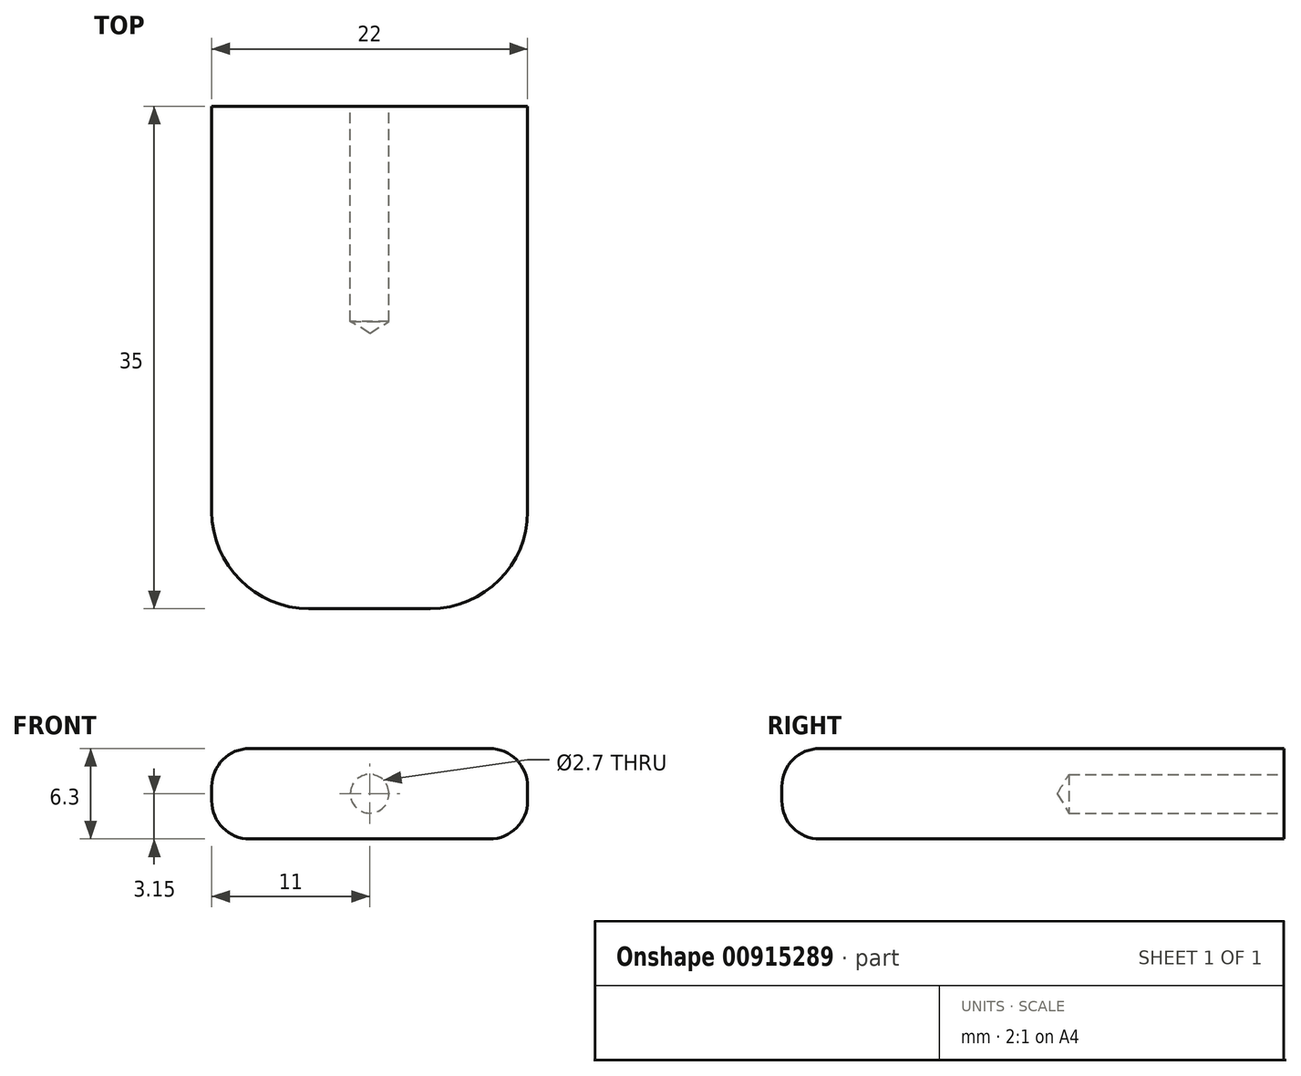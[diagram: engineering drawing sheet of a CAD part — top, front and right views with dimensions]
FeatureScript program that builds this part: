
annotation { "Feature Type Name" : "Feature", "Feature Type Description" : "" }
export const myFeature = defineFeature(function(context is Context, id is Id, definition is map)
    precondition{}
    {
        {
            var Q0;
            Q0=qCreatedBy(makeId("Top.planeOp"),FACE);
            var sketch = newSketch(context, id + "F0", { "sketchPlane" : qUnion([Q0])});
            skLineSegment(sketch, "E0.bottom", {"start": v(11, -17.5) * mm, "end": v(-11, -17.5) * mm});
            skLineSegment(sketch, "E0.top", {"start": v(11, 17.5) * mm, "end": v(-11, 17.5) * mm});
            skLineSegment(sketch, "E0.left", {"start": v(11, -17.5) * mm, "end": v(11, 17.5) * mm});
            skLineSegment(sketch, "E0.right", {"start": v(-11, -17.5) * mm, "end": v(-11, 17.5) * mm});
            skPoint(sketch, "E0.middle", {"position": v(0, 0) * mm});
            skSolve(sketch);
        }
        {
            var Q0;
            Q0 = qSketchRegion(id + "F0", true);
            extrude(context, id + "F1", {"entities" : qUnion([Q0]), "depth" : 6.3 * mm, "offsetDistance" : 25 * mm});
        }
        {
            var Q0;
            Q0=makeQuery(id+"F1.opExtrude","SWEPT_EDGE",EDGE,{"disambiguationData":[OSD([sQuery(id+"F0.wireOp",EDGE,"E0.bottom"),sQuery(id+"F0.wireOp",EDGE,"E0.right")])]});
            var Q1;
            Q1=makeQuery(id+"F1.opExtrude","SWEPT_EDGE",EDGE,{"disambiguationData":[OSD([sQuery(id+"F0.wireOp",EDGE,"E0.bottom"),sQuery(id+"F0.wireOp",EDGE,"E0.left")])]});
            fillet(context, id + "F2", {"entities" : qUnion([Q0, Q1]), "radius" : 6.76 * mm, "tangentPropagation" : true, "allowEdgeOverflow" : false});
        }
        {
            var Q0;
            Q0=makeQuery(id+"F1.opExtrude","CAP_EDGE",EDGE,{"disambiguationData":[OSD([sQuery(id+"F0.wireOp",EDGE,"E0.right")])],"isStart":false});
            var Q1;
            Q1=makeQuery(id+"F1.opExtrude","CAP_EDGE",EDGE,{"disambiguationData":[OSD([sQuery(id+"F0.wireOp",EDGE,"E0.right")])],"isStart":true});
            fillet(context, id + "F3", {"entities" : qUnion([Q0, Q1]), "radius" : 2.65 * mm, "tangentPropagation" : true, "allowEdgeOverflow" : false});
        }
        {
            var Q0;
            Q0=makeQuery(id+"F1.opExtrude","SWEPT_FACE",FACE,{"disambiguationData":[OSD([sQuery(id+"F0.wireOp",EDGE,"E0.top")])]});
            var sketch = newSketch(context, id + "F4", { "sketchPlane" : qUnion([Q0])});
            skLineSegment(sketch, "E1", {"start": v(0, 0) * mm, "end": v(0, 6.3) * mm, "construction": true});
            skPoint(sketch, "E2", {"position": v(0, 3.15) * mm});
            skCircle(sketch, "E3", {"center": v(0, 3.15) * mm, "radius": 1.35 * mm, "construction": true});
            skSolve(sketch);
        }
        {
            var Q0;
            Q0=sQuery(id+"F4.wireOp",VERTEX,"E2");
            var Q1;
            Q1=makeQuery(id+"F1.opExtrude","SWEPT_BODY",BODY,{"disambiguationData":[OSD([sQuery(id+"F0.wireOp",EDGE,"E0.bottom"),sQuery(id+"F0.wireOp",EDGE,"E0.top"),sQuery(id+"F0.wireOp",EDGE,"E0.left"),sQuery(id+"F0.wireOp",EDGE,"E0.right")])]});
            hole(context, id + "F5", {"style" : HoleStyle.SIMPLE, "endStyle" : HoleEndStyle.BLIND, "holeDiameter" : 2.7 * mm, "majorDiameter" : 5 * mm, "holeDepth" : 15 * mm, "isTappedThrough" : true, "tappedDepth" : 12 * mm, "tapClearance" : 3, "locations" : qUnion([Q0]), "scope" : qUnion([Q1])});
        }
    });
